# Revit family: KM4-Wall Mount
name_source: partatom
category: Lighting Fixtures
revit_build: Autodesk Revit 2013 (Build: 20120221_2030(x64)
units: mm (PartAtom-declared; Revit-internal decimal feet)

## types (1)
- KM41-Wall Mount
    Apparent Load = 24 VA
    Assembly Code = D5020280
    Default Elevation = 48 "
    Description = KM4 is the most compact version of KicK and is ideal for even the most discrete architectural applications
    Finish = Hubbell-Titanium
    Glass = Hubbell-Glass
    Lamp = LED
    Load Classification = Lighting
    Manufacturer = Architectural Area Lighting
    Manufacturer Fax = 626-369-2695
    Model = KicK™ Mini Small-Wall Mount
    Photometrics Web = Web K4 : KM4-T4-2050
    Power Factor = 1
    Product Documentation Link = http://www.aal.net
    Product Page URL = http://www.aal.net
    URL = http://www.aal.net
    Voltage = 120 V
    Watts = 24 W

## geometry (parser evidence)
native form markers: Blend x36, Sweep x5
no freeform markers — native parametric forms only
